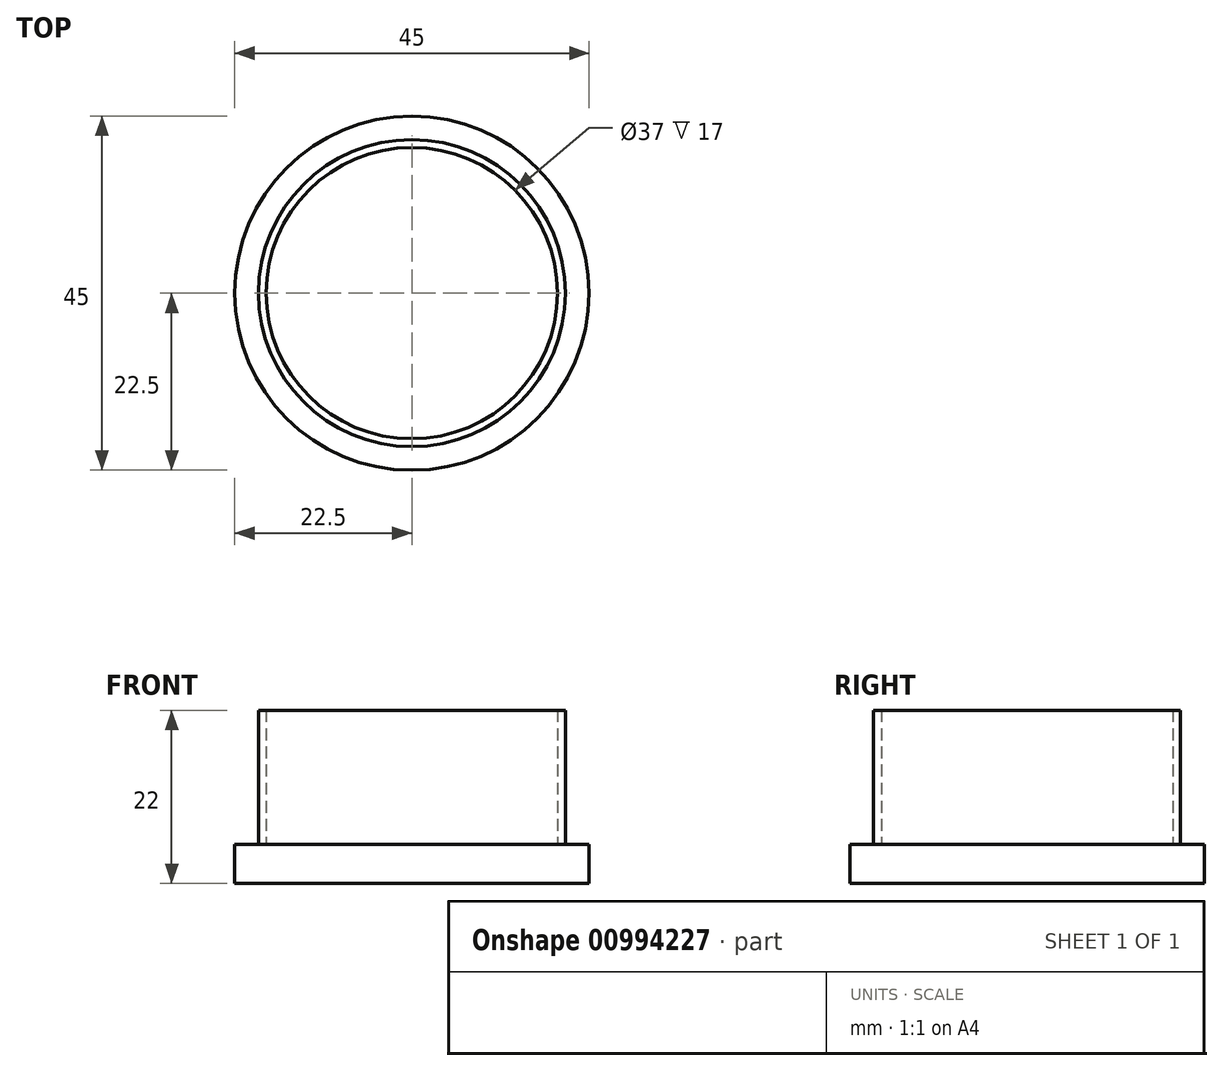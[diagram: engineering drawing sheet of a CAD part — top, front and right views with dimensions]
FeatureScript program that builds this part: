
annotation { "Feature Type Name" : "Feature", "Feature Type Description" : "" }
export const myFeature = defineFeature(function(context is Context, id is Id, definition is map)
    precondition{}
    {
        {
            var Q0;
            Q0=qCreatedBy(makeId("Top.planeOp"),FACE);
            var sketch = newSketch(context, id + "F0", { "sketchPlane" : qUnion([Q0])});
            skCircle(sketch, "E0", {"center": v(0, 0) * mm, "radius": 22.5 * mm});
            skSolve(sketch);
        }
        {
            var Q0;
            Q0=makeQuery(id+"F0.imprint","IMPRINT",FACE,{"disambiguationData":[TD([[makeQuery(id+"F0.imprint","IMPRINT",EDGE,{"derivedFrom":sQuery(id+"F0.wireOp",EDGE,"E0")}),1.0]])]});
            extrude(context, id + "F1", {"entities" : qUnion([Q0]), "depth" : 5 * mm, "offsetDistance" : 25 * mm});
        }
        {
            var Q0;
            Q0=qCreatedBy(makeId("Top.planeOp"),FACE);
            var sketch = newSketch(context, id + "F2", { "sketchPlane" : qUnion([Q0])});
            skCircle(sketch, "E1", {"center": v(0, 0) * mm, "radius": 19.5 * mm});
            skCircle(sketch, "E2", {"center": v(0, 0) * mm, "radius": 18.5 * mm});
            skSolve(sketch);
        }
        {
            var Q0;
            Q0=makeQuery(id+"F2.imprint","IMPRINT",FACE,{"disambiguationData":[TD([[makeQuery(id+"F2.imprint","IMPRINT",EDGE,{"derivedFrom":sQuery(id+"F2.wireOp",EDGE,"E1")}),1.0]])]});
            extrude(context, id + "F3", {"entities" : qUnion([Q0]), "operationType" : NewBodyOperationType.ADD, "depth" : 22 * mm, "offsetDistance" : 25 * mm});
        }
    });
